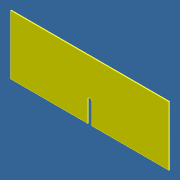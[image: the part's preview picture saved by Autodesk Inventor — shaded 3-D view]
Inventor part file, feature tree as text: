
AUTODESK INVENTOR PART (.ipt)
format: ipt  version: 2012 (Build 160160000, 160)  size: 69,632 bytes
history: native  units: in
note: dims shown in document units (in); Inventor stores cm internally (conversion verified against a paired STEP export)
features: extrude x1, sketch x1
ambient origin geometry x8: Origin, YZ Plane, XZ Plane, XY Plane, X Axis, Y Axis, Z Axis, Center Point
bodies: Solid1 (feature_tree)
feature tree (2):
  extrude  "Extrusion1"  Depth=9.0in
  sketch  "Sketch1"  dims[d0=24.0in d1=9.0in d2=0.625in d3=12.0in d4=3.1875in d5=0.125in d6=0.0in]
